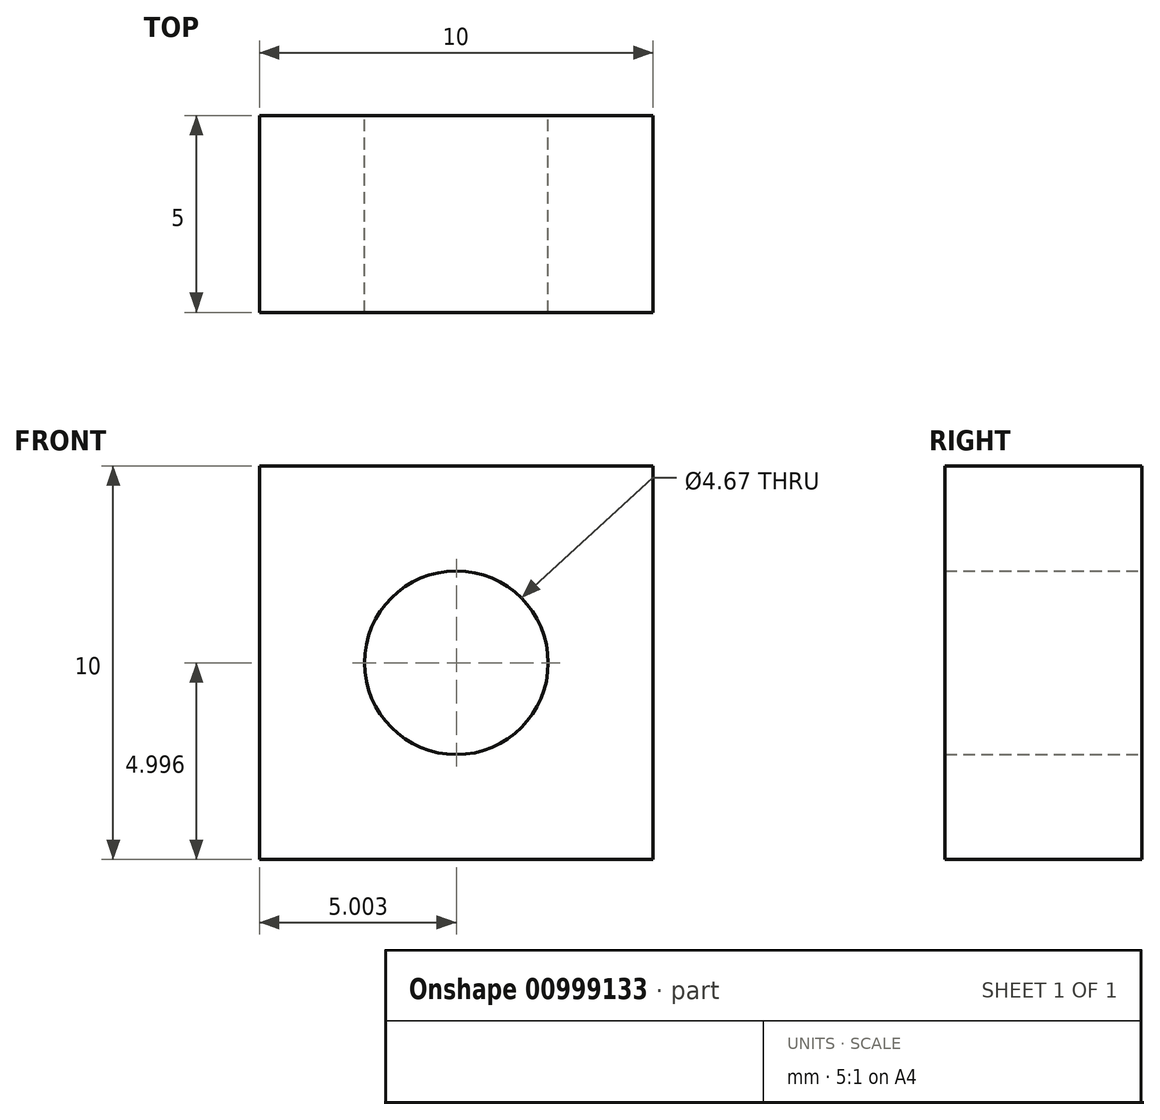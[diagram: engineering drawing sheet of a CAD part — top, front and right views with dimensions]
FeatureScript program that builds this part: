
annotation { "Feature Type Name" : "Feature", "Feature Type Description" : "" }
export const myFeature = defineFeature(function(context is Context, id is Id, definition is map)
    precondition{}
    {
        {
            var Q0;
            Q0=qCreatedBy(makeId("Front.planeOp"),FACE);
            var sketch = newSketch(context, id + "F0", { "sketchPlane" : qUnion([Q0])});
            skLineSegment(sketch, "E0.bottom", {"start": v(-3.48, -1.25) * mm, "end": v(6.52, -1.25) * mm});
            skLineSegment(sketch, "E0.top", {"start": v(-3.48, -11.25) * mm, "end": v(6.52, -11.25) * mm});
            skLineSegment(sketch, "E0.left", {"start": v(-3.48, -1.25) * mm, "end": v(-3.48, -11.25) * mm});
            skLineSegment(sketch, "E0.right", {"start": v(6.52, -1.25) * mm, "end": v(6.52, -11.25) * mm});
            skPoint(sketch, "E1", {"position": v(-3.48, -6.25) * mm});
            skPoint(sketch, "E2", {"position": v(1.52, -11.25) * mm});
            skLineSegment(sketch, "E3", {"start": v(-3.48, -6.25) * mm, "end": v(10.84, -6.25) * mm, "construction": true});
            skLineSegment(sketch, "E4", {"start": v(1.52, -11.25) * mm, "end": v(1.52, 9.01) * mm, "construction": true});
            skCircle(sketch, "E5", {"center": v(1.52, -6.25) * mm, "radius": 2.33 * mm});
            skPoint(sketch, "E6", {"position": v(3.52, -5.05) * mm});
            skSolve(sketch);
        }
        {
            var Q0;
            Q0=makeQuery(id+"F0.imprint","IMPRINT",FACE,{"disambiguationData":[TD([[makeQuery(id+"F0.imprint","IMPRINT",EDGE,{"derivedFrom":sQuery(id+"F0.wireOp",EDGE,"E0.bottom")}),-1.0]])]});
            extrude(context, id + "F1", {"entities" : qUnion([Q0]), "depth" : 5 * mm, "offsetDistance" : 25 * mm});
        }
    });
